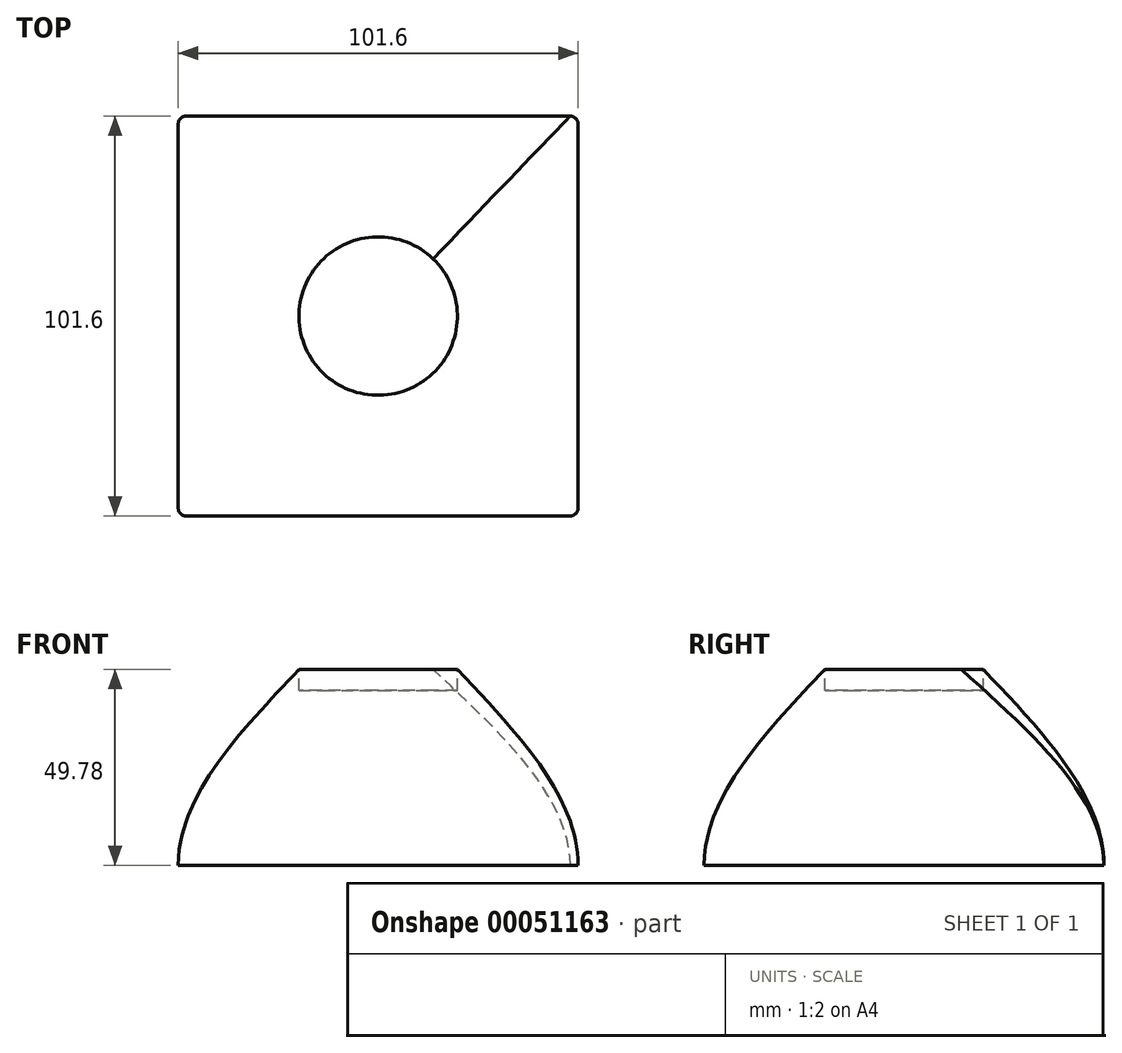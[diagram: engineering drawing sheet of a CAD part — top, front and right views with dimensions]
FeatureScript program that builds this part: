
annotation { "Feature Type Name" : "Feature", "Feature Type Description" : "" }
export const myFeature = defineFeature(function(context is Context, id is Id, definition is map)
    precondition{}
    {
        {
            var Q0;
            Q0=qCreatedBy(makeId("Top.planeOp"),FACE);
            var sketch = newSketch(context, id + "F0", { "sketchPlane" : qUnion([Q0])});
            skLineSegment(sketch, "E0.rect.bottom", {"start": v(48.8, 50.8) * mm, "end": v(-48.8, 50.8) * mm});
            skLineSegment(sketch, "E0.rect.top", {"start": v(48.8, -50.8) * mm, "end": v(-48.8, -50.8) * mm});
            skLineSegment(sketch, "E0.rect.left", {"start": v(50.8, 48.8) * mm, "end": v(50.8, -48.8) * mm});
            skLineSegment(sketch, "E0.rect.right", {"start": v(-50.8, 48.8) * mm, "end": v(-50.8, -48.8) * mm});
            skPoint(sketch, "E0.rect.middle", {"position": v(0, 0) * mm});
            skArc(sketch, "E1", {"start": v(-48.8, 50.8) * mm, "mid": v(-50.21, 50.21) * mm, "end": v(-50.8, 48.8) * mm});
            skPoint(sketch, "E2.orphan", {"position": v(-50.8, 50.8) * mm});
            skArc(sketch, "E3", {"start": v(50.8, 48.8) * mm, "mid": v(50.21, 50.21) * mm, "end": v(48.8, 50.8) * mm});
            skArc(sketch, "E4", {"start": v(48.8, -50.8) * mm, "mid": v(50.21, -50.21) * mm, "end": v(50.8, -48.8) * mm});
            skArc(sketch, "E5", {"start": v(-50.8, -48.8) * mm, "mid": v(-50.21, -50.21) * mm, "end": v(-48.8, -50.8) * mm});
            skPoint(sketch, "E6.orphan", {"position": v(50.8, 50.8) * mm});
            skPoint(sketch, "E7.orphan", {"position": v(50.8, -50.8) * mm});
            skPoint(sketch, "E8.orphan", {"position": v(-50.8, -50.8) * mm});
            skSolve(sketch);
        }
        {
            var Q0;
            Q0=qCreatedBy(makeId("Top.planeOp"),FACE);
            cPlane(context, id + "F1", {"entities" : qUnion([Q0]), "cplaneType" : CPlaneType.OFFSET, "offset" : 49.78 * mm, "width" : 150 * mm, "height" : 150 * mm});
        }
        {
            var Q0;
            Q0=qCreatedBy(id+"F1.planeOp",FACE);
            var sketch = newSketch(context, id + "F2", { "sketchPlane" : qUnion([Q0])});
            skCircle(sketch, "E9", {"center": v(0, 0) * mm, "radius": 20.13 * mm});
            skSolve(sketch);
        }
        {
            var Q0;
            Q0 = qSketchRegion(id + "F0", true);
            var Q1;
            Q1 = qSketchRegion(id + "F2", true);
            loft(context, id + "F3", {"startCondition" : LoftEndDerivativeType.NORMAL_TO_PROFILE, "startMagnitude" : 1, "sheetProfilesArray" : [{ "sheetProfileEntities" : qUnion([Q0]) }, { "sheetProfileEntities" : qUnion([Q1]) }]});
        }
        {
            var Q0;
            Q0=makeQuery(id+"F3.opLoft","CAP_FACE",FACE,{"disambiguationData":[OSD([makeQuery(id+"F2.imprint","IMPRINT",FACE,{"disambiguationData":[TD([[makeQuery(id+"F2.imprint","IMPRINT",EDGE,{"derivedFrom":sQuery(id+"F2.wireOp",EDGE,"E9")}),1.0]])]})])],"isStart":true});
            var sketch = newSketch(context, id + "F4", { "sketchPlane" : qUnion([Q0])});
            skCircle(sketch, "E10", {"center": v(0, 0) * mm, "radius": 20.64 * mm});
            skSolve(sketch);
        }
        {
            var Q0;
            {var subQ0=sQuery(id+"F2.wireOp",EDGE,"E9");var subQ3=sQuery(id+"F0.wireOp",EDGE,"E0.rect.bottom");var subQ4=sQuery(id+"F0.wireOp",EDGE,"E3");Q0=makeQuery(id+"F4.imprint","IMPRINT",FACE,{"disambiguationData":[TD([[makeQuery(id+"F4.imprint","IMPRINT",EDGE,{"derivedFrom":makeQuery(id+"F3.opLoft","MID_CAP_EDGE",EDGE,{"disambiguationData":[OSD([subQ3,subQ4,subQ0])],"capPos":1.0})}),1.0]])]});}
            extrude(context, id + "F5", {"entities" : qUnion([Q0]), "operationType" : NewBodyOperationType.REMOVE, "oppositeDirection" : true, "depth" : 5.3 * mm});
        }
        {
            var Q0;
            Q0=makeQuery(id+"F5.boolean.opBoolean","COPY",FACE,{"derivedFrom":makeQuery(id+"F5.opExtrude","CAP_FACE",FACE,{"disambiguationData":[OSD([sQuery(id+"F0.wireOp",EDGE,"E0.rect.bottom"),sQuery(id+"F0.wireOp",EDGE,"E0.rect.top"),sQuery(id+"F0.wireOp",EDGE,"E0.rect.left"),sQuery(id+"F0.wireOp",EDGE,"E0.rect.right"),sQuery(id+"F0.wireOp",EDGE,"E1"),sQuery(id+"F0.wireOp",EDGE,"E3"),sQuery(id+"F0.wireOp",EDGE,"E4"),sQuery(id+"F0.wireOp",EDGE,"E5"),sQuery(id+"F2.wireOp",EDGE,"E9")])],"isStart":false})});
            cPlane(context, id + "F6", {"entities" : qUnion([Q0]), "cplaneType" : CPlaneType.OFFSET, "offset" : 1 / 203.2 * mm, "oppositeDirection" : true, "width" : 150 * mm, "height" : 150 * mm});
        }
    });
